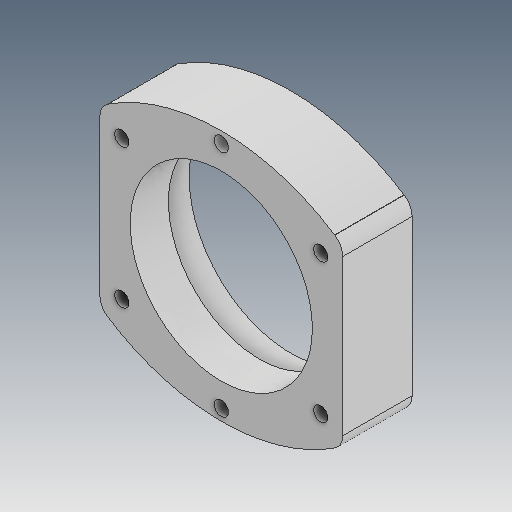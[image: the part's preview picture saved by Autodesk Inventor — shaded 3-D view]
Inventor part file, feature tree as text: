
AUTODESK INVENTOR PART (.ipt)
format: ipt  version: 2020.3 (Build 243373010, 373A)  size: 147,968 bytes
history: native  units: mm
features: extrude x2, sketch x2
ambient origin geometry x8: Origin, YZ Plane, XZ Plane, XY Plane, X Axis, Y Axis, Z Axis, Center Point
bodies: Solid1 (feature_tree)
feature tree (4):
  extrude  "Extrusion1"  Depth=33.0mm
  extrude  "Extrusion2"  Depth=9.0mm
  sketch  "Sketch1"  dims[d0=20.0mm d1=0.0mm d2=33.0mm]
  sketch  "Sketch2"  dims[d3=33.0mm d4=58.525mm d5=9.0mm d6=0.0mm]
